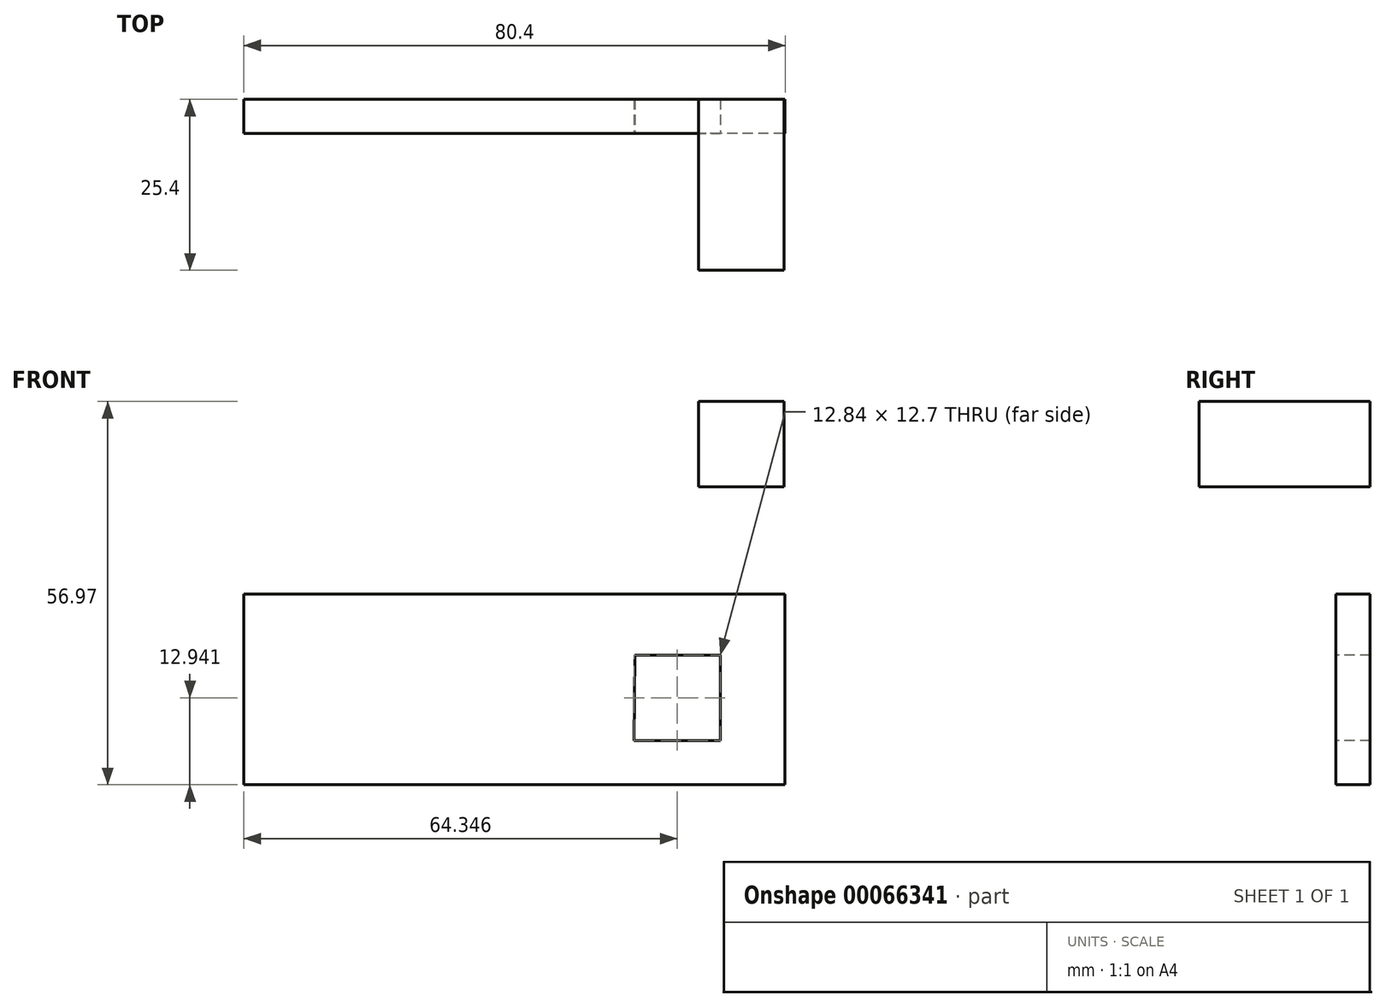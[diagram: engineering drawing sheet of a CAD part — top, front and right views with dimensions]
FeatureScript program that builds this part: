
annotation { "Feature Type Name" : "Feature", "Feature Type Description" : "" }
export const myFeature = defineFeature(function(context is Context, id is Id, definition is map)
    precondition{}
    {
        {
            var Q0;
            Q0=qCreatedBy(makeId("Front.planeOp"),FACE);
            var sketch = newSketch(context, id + "F0", { "sketchPlane" : qUnion([Q0])});
            skLineSegment(sketch, "E0", {"start": v(48.94, 0) * mm, "end": v(48.94, 28.35) * mm});
            skLineSegment(sketch, "E1", {"start": v(48.94, 28.35) * mm, "end": v(-31.46, 28.35) * mm});
            skLineSegment(sketch, "E2", {"start": v(-31.46, 28.35) * mm, "end": v(-31.46, 0) * mm});
            skLineSegment(sketch, "E3", {"start": v(-31.46, 0) * mm, "end": v(48.94, 0) * mm});
            skSolve(sketch);
        }
        {
            var Q0;
            Q0 = qSketchRegion(id + "F0", true);
            extrude(context, id + "F1", {"entities" : qUnion([Q0]), "depth" : 5.08 * mm});
        }
        {
            var Q0;
            Q0=makeQuery(id+"F1.opExtrude","CAP_FACE",FACE,{"disambiguationData":[OSD([sQuery(id+"F0.wireOp",EDGE,"E0"),sQuery(id+"F0.wireOp",EDGE,"E1"),sQuery(id+"F0.wireOp",EDGE,"E2"),sQuery(id+"F0.wireOp",EDGE,"E3")])],"isStart":false});
            var sketch = newSketch(context, id + "F2", { "sketchPlane" : qUnion([Q0])});
            skLineSegment(sketch, "E4", {"start": v(26.47, 6.6) * mm, "end": v(39.3, 6.6) * mm});
            skLineSegment(sketch, "E5", {"start": v(39.3, 6.6) * mm, "end": v(39.3, 19.3) * mm});
            skLineSegment(sketch, "E6", {"start": v(39.3, 19.3) * mm, "end": v(26.6, 19.3) * mm});
            skLineSegment(sketch, "E7", {"start": v(26.6, 19.3) * mm, "end": v(26.47, 6.6) * mm});
            skSolve(sketch);
        }
        {
            var Q0;
            Q0 = qSketchRegion(id + "F2", true);
            extrude(context, id + "F3", {"entities" : qUnion([Q0]), "operationType" : NewBodyOperationType.REMOVE, "oppositeDirection" : true, "depth" : 5.08 * mm});
        }
        {
            var Q0;
            Q0=qCreatedBy(makeId("Front.planeOp"),FACE);
            var sketch = newSketch(context, id + "F4", { "sketchPlane" : qUnion([Q0])});
            skLineSegment(sketch, "E8", {"start": v(36.05, 56.97) * mm, "end": v(36.05, 44.27) * mm});
            skLineSegment(sketch, "E9", {"start": v(36.05, 44.27) * mm, "end": v(48.75, 44.27) * mm});
            skLineSegment(sketch, "E10", {"start": v(48.75, 44.27) * mm, "end": v(48.75, 56.97) * mm});
            skLineSegment(sketch, "E11", {"start": v(48.75, 56.97) * mm, "end": v(36.05, 56.97) * mm});
            skSolve(sketch);
        }
        {
            var Q0;
            Q0 = qSketchRegion(id + "F4", true);
            extrude(context, id + "F5", {"entities" : qUnion([Q0]), "depth" : 25.4 * mm});
        }
    });
